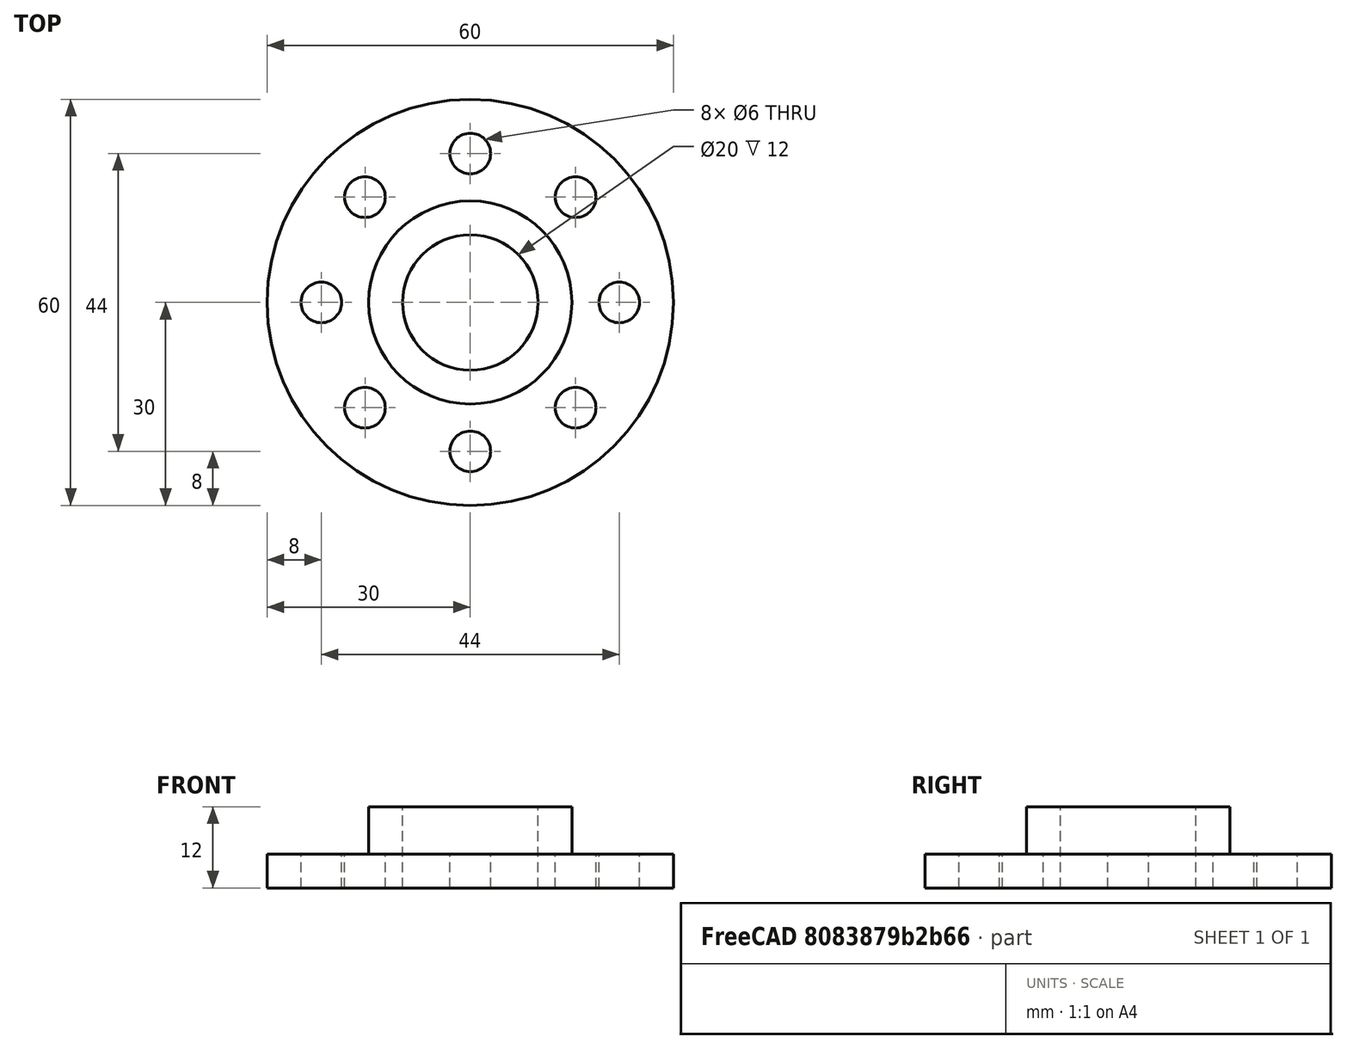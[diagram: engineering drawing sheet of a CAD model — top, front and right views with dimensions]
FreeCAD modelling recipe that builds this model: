
FCSTD DOCUMENT  (FreeCAD 0.18.4R)
Label: tutorial_freecad_ex11_a
License: All rights reserved
LicenseURL: http://en.wikipedia.org/wiki/All_rights_reserved
objects: Part::Cylinder×4, Part::Cut×2, Part::MultiFuse×1, Part::FeaturePython×1
note: 8 computed .brp shape members not serialized (recipe doc carries the construction recipe); baked Part::Feature solids carry a one-line shape summary decoded from their .brp

FEATURE [Part::Cylinder] Cylinder  label="base"
  Angle = 360
  AttacherType = Attacher::AttachEngine3D
  Height = 5
  Radius = 30
FEATURE [Part::Cylinder] Cylinder001  label="tubo exterior"
  Angle = 360
  AttacherType = Attacher::AttachEngine3D
  Height = 12
  Radius = 15
FEATURE [Part::MultiFuse] Fusion
  Refine = true
  Shapes = -> [Cylinder,Cylinder001]
FEATURE [Part::Cylinder] Cylinder002  label="Cilindro"
  Angle = 360
  AttacherType = Attacher::AttachEngine3D
  Height = 30
  Placement = pos=(0,0,-2) rot=(0,0,1;0rad)
  Radius = 10
FEATURE [Part::Cut] Cut  label="brida sin taladros"
  Base = -> Fusion
  Refine = true
  Tool = -> Cylinder002
FEATURE [Part::Cylinder] Cylinder003  label="taladro_master"
  Angle = 360
  AttacherType = Attacher::AttachEngine3D
  Height = 10
  Placement = pos=(22,0,-2) rot=(0,0,1;0rad)
  Radius = 3
FEATURE [Part::FeaturePython] Array  # Draft array (typed FeaturePython)
  Angle = 360
  ArrayType = 1
  Axis = (0,0,1)
  Base = -> Cylinder003
  Center = (0,0,0)
  Fuse = false
  IntervalAxis = (0,0,0)
  IntervalX = (1,0,0)
  IntervalY = (0,1,0)
  IntervalZ = (0,0,1)
  NumberPolar = 8
  NumberX = 2
  NumberY = 2
  NumberZ = 1
FEATURE [Part::Cut] Cut001
  Base = -> Cut
  Refine = true
  Tool = -> Array
